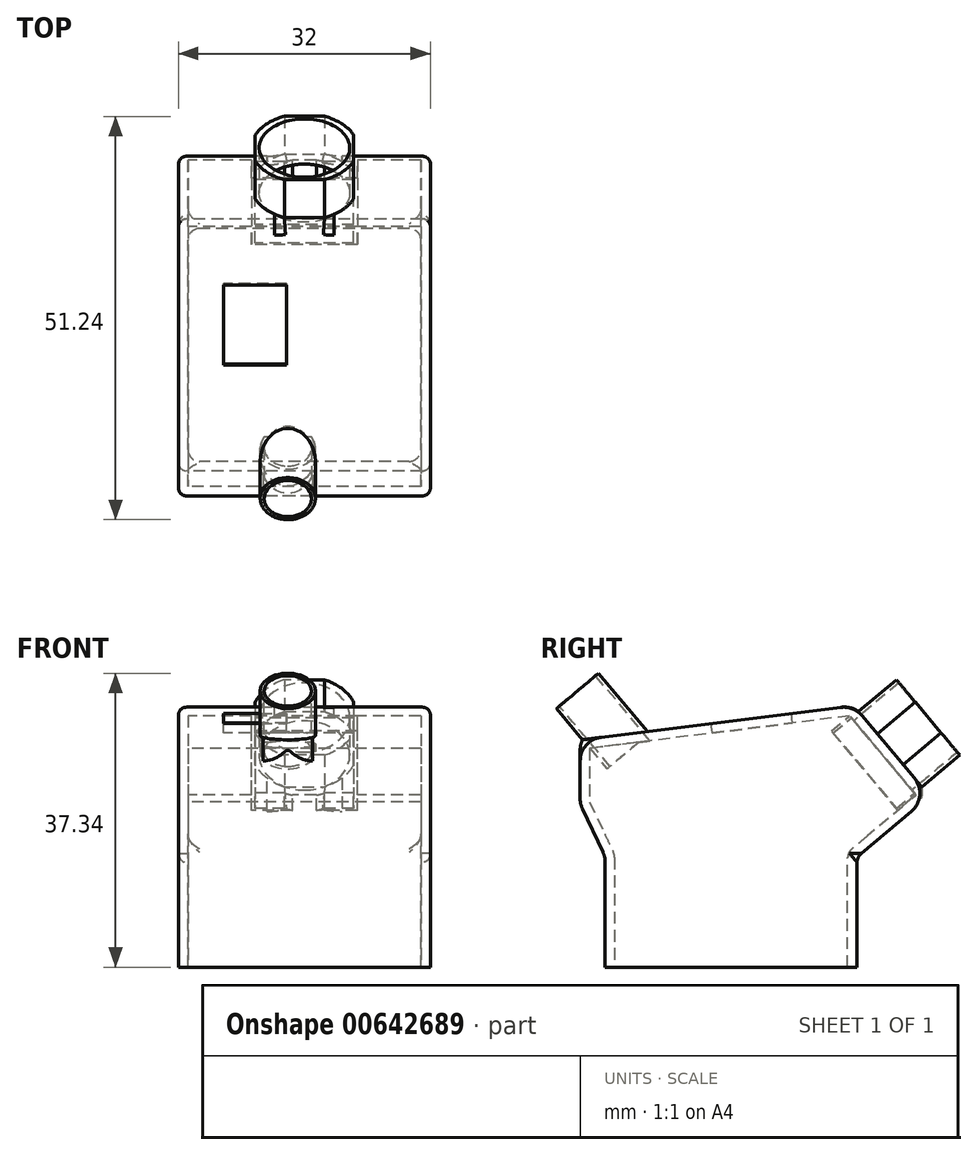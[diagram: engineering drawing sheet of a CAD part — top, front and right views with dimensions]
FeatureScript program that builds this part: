
annotation { "Feature Type Name" : "Feature", "Feature Type Description" : "" }
export const myFeature = defineFeature(function(context is Context, id is Id, definition is map)
    precondition{}
    {
        {
            var Q0;
            Q0=qCreatedBy(makeId("Right.planeOp"),FACE);
            var sketch = newSketch(context, id + "F0", { "sketchPlane" : qUnion([Q0])});
            skLineSegment(sketch, "E0", {"start": v(-20.8, -5.59) * mm, "end": v(11.2, -5.59) * mm});
            skLineSegment(sketch, "E1", {"start": v(11.2, -5.59) * mm, "end": v(11.2, 8.41) * mm});
            skLineSegment(sketch, "E2", {"start": v(-20.8, 8.41) * mm, "end": v(-20.8, -5.59) * mm});
            skLineSegment(sketch, "E3", {"start": v(10.74, 27.62) * mm, "end": v(20.39, 16.12) * mm});
            skLineSegment(sketch, "E4", {"start": v(20.39, 16.12) * mm, "end": v(11.2, 8.41) * mm});
            skLineSegment(sketch, "E5", {"start": v(-20.8, 8.41) * mm, "end": v(23.26, 8.41) * mm, "construction": true});
            skLineSegment(sketch, "E6", {"start": v(10.74, 27.62) * mm, "end": v(-23.98, 23.26) * mm});
            skLineSegment(sketch, "E7", {"start": v(-23.98, 23.26) * mm, "end": v(-23.98, 15.14) * mm});
            skLineSegment(sketch, "E8", {"start": v(-23.98, 15.14) * mm, "end": v(-20.8, 8.41) * mm});
            skSolve(sketch);
        }
        {
            var Q0;
            Q0=makeQuery(id+"F0.imprint","IMPRINT",FACE,{"disambiguationData":[TD([[makeQuery(id+"F0.imprint","IMPRINT",EDGE,{"derivedFrom":sQuery(id+"F0.wireOp",EDGE,"E0")}),1.0]])]});
            extrude(context, id + "F1", {"entities" : qUnion([Q0]), "depth" : 32 * mm, "offsetDistance" : 25 * mm});
        }
        {
            var Q0;
            Q0=makeQuery(id+"F1.opExtrude","SWEPT_FACE",FACE,{"disambiguationData":[OSD([sQuery(id+"F0.wireOp",EDGE,"E0")])]});
            shell(context, id + "F2", {"entities" : qUnion([Q0]), "thickness" : 1.2 * mm});
        }
        {
            var Q0;
            Q0=makeQuery(id+"F2.opShell","OFFSET_FACE",FACE,{"disambiguationData":[OSD([sQuery(id+"F0.wireOp",EDGE,"E3")])]});
            var sketch = newSketch(context, id + "F3", { "sketchPlane" : qUnion([Q0])});
            skCircle(sketch, "E9", {"center": v(16, 7.02) * mm, "radius": 5.75 * mm});
            skPoint(sketch, "E9.centerSnap0", {"position": v(16, 13.6) * mm});
            skPoint(sketch, "E9.centerSnap1", {"position": v(1.2, 7.02) * mm});
            skCircle(sketch, "E10.0", {"center": v(16, 7.02) * mm, "radius": 6.75 * mm});
            skLineSegment(sketch, "E11.0", {"start": v(-3.8, 18.6) * mm, "end": v(-3.8, -4.55) * mm});
            skLineSegment(sketch, "E11.1", {"start": v(35.8, 18.6) * mm, "end": v(-3.8, 18.6) * mm});
            skLineSegment(sketch, "E11.2", {"start": v(35.8, -4.55) * mm, "end": v(35.8, 18.6) * mm});
            skLineSegment(sketch, "E11.3", {"start": v(-3.8, -4.55) * mm, "end": v(35.8, -4.55) * mm});
            skLineSegment(sketch, "E12.bottom", {"start": v(22.25, 13.27) * mm, "end": v(9.75, 13.27) * mm});
            skLineSegment(sketch, "E12.top", {"start": v(22.25, 0.77) * mm, "end": v(9.75, 0.77) * mm});
            skLineSegment(sketch, "E12.left", {"start": v(22.25, 13.27) * mm, "end": v(22.25, 0.77) * mm});
            skLineSegment(sketch, "E12.right", {"start": v(9.75, 13.27) * mm, "end": v(9.75, 0.77) * mm});
            skLineSegment(sketch, "E13.bottom", {"start": v(22.75, 0.27) * mm, "end": v(9.25, 0.27) * mm});
            skLineSegment(sketch, "E13.top", {"start": v(22.75, 13.77) * mm, "end": v(9.25, 13.77) * mm});
            skLineSegment(sketch, "E13.left", {"start": v(22.75, 0.27) * mm, "end": v(22.75, 13.77) * mm});
            skLineSegment(sketch, "E13.right", {"start": v(9.25, 0.27) * mm, "end": v(9.25, 13.77) * mm});
            skSolve(sketch);
        }
        {
            var Q0;
            Q0=makeQuery(id+"F3.imprint","IMPRINT",FACE,{"disambiguationData":[TD([[makeQuery(id+"F3.imprint","IMPRINT",EDGE,{"derivedFrom":sQuery(id+"F3.wireOp",EDGE,"E9")}),1.0]])]});
            extrude(context, id + "F4", {"entities" : qUnion([Q0]), "operationType" : NewBodyOperationType.REMOVE, "oppositeDirection" : true, "depth" : 25 * mm, "offsetDistance" : 25 * mm});
        }
        {
            var Q0;
            Q0=makeQuery(id+"F3.imprint","IMPRINT",FACE,{"disambiguationData":[TD([[makeQuery(id+"F3.imprint","IMPRINT",EDGE,{"derivedFrom":sQuery(id+"F3.wireOp",EDGE,"E9")}),-1.0]])]});
            extrude(context, id + "F5", {"entities" : qUnion([Q0]), "operationType" : NewBodyOperationType.ADD, "oppositeDirection" : true, "depth" : 7.5 * mm, "offsetDistance" : 25 * mm});
        }
        {
            var Q0;
            Q0=makeQuery(id+"F1.opExtrude","SWEPT_EDGE",EDGE,{"disambiguationData":[OSD([sQuery(id+"F0.wireOp",EDGE,"E6"),sQuery(id+"F0.wireOp",EDGE,"E7")])]});
            cPlane(context, id + "F6", {"entities" : qUnion([Q0]), "cplaneType" : CPlaneType.LINE_ANGLE, "offset" : 25 * mm, "angle" : 50 * degree, "width" : 150 * mm, "height" : 150 * mm});
        }
        {
            var Q0;
            Q0=qCreatedBy(id+"F6.planeOp",FACE);
            var sketch = newSketch(context, id + "F7", { "sketchPlane" : qUnion([Q0])});
            skCircle(sketch, "E14", {"center": v(13.89, 0.33) * mm, "radius": 3 * mm});
            skCircle(sketch, "E15", {"center": v(13.89, 0.33) * mm, "radius": 3.5 * mm});
            skSolve(sketch);
        }
        {
            var Q0;
            Q0=makeQuery(id+"F7.imprint","IMPRINT",FACE,{"disambiguationData":[TD([[makeQuery(id+"F7.imprint","IMPRINT",EDGE,{"derivedFrom":sQuery(id+"F7.wireOp",EDGE,"E14")}),1.0]])]});
            extrude(context, id + "F8", {"entities" : qUnion([Q0]), "operationType" : NewBodyOperationType.REMOVE, "oppositeDirection" : true, "depth" : 10 * mm, "offsetDistance" : 25 * mm});
        }
        {
            var Q0;
            Q0=makeQuery(id+"F7.imprint","IMPRINT",FACE,{"disambiguationData":[TD([[makeQuery(id+"F7.imprint","IMPRINT",EDGE,{"derivedFrom":sQuery(id+"F7.wireOp",EDGE,"E14")}),-1.0]])]});
            extrude(context, id + "F9", {"entities" : qUnion([Q0]), "operationType" : NewBodyOperationType.ADD, "endBound" : BoundingType.SYMMETRIC, "depth" : 10 * mm, "offsetDistance" : 25 * mm});
        }
        {
            var Q0;
            Q0=makeQuery(id+"F1.opExtrude","SWEPT_EDGE",EDGE,{"disambiguationData":[OSD([sQuery(id+"F0.wireOp",EDGE,"E3"),sQuery(id+"F0.wireOp",EDGE,"E6")])]});
            var Q1;
            Q1=makeQuery(id+"F1.opExtrude","SWEPT_EDGE",EDGE,{"disambiguationData":[OSD([sQuery(id+"F0.wireOp",EDGE,"E3"),sQuery(id+"F0.wireOp",EDGE,"E4")])]});
            var Q2;
            Q2=makeQuery(id+"F1.opExtrude","SWEPT_EDGE",EDGE,{"disambiguationData":[OSD([sQuery(id+"F0.wireOp",EDGE,"E2"),sQuery(id+"F0.wireOp",EDGE,"E8")])]});
            var Q3;
            Q3=makeQuery(id+"F1.opExtrude","SWEPT_EDGE",EDGE,{"disambiguationData":[OSD([sQuery(id+"F0.wireOp",EDGE,"E7"),sQuery(id+"F0.wireOp",EDGE,"E8")])]});
            var Q4;
            Q4=makeQuery(id+"F1.opExtrude","SWEPT_EDGE",EDGE,{"disambiguationData":[OSD([sQuery(id+"F0.wireOp",EDGE,"E6"),sQuery(id+"F0.wireOp",EDGE,"E7")])]});
            fillet(context, id + "F10", {"entities" : qUnion([Q0, Q1, Q2, Q3, Q4]), "radius" : 3 * mm, "tangentPropagation" : true, "allowEdgeOverflow" : false});
        }
        {
            var Q0;
            Q0=makeQuery(id+"F1.opExtrude","CAP_EDGE",EDGE,{"disambiguationData":[OSD([sQuery(id+"F0.wireOp",EDGE,"E1")])],"isStart":true});
            var Q1;
            Q1=makeQuery(id+"F1.opExtrude","CAP_EDGE",EDGE,{"disambiguationData":[OSD([sQuery(id+"F0.wireOp",EDGE,"E4")])],"isStart":true});
            var Q2;
            Q2=makeQuery(id+"F1.opExtrude","CAP_EDGE",EDGE,{"disambiguationData":[OSD([sQuery(id+"F0.wireOp",EDGE,"E1")])],"isStart":false});
            var Q3;
            Q3=makeQuery(id+"F1.opExtrude","CAP_EDGE",EDGE,{"disambiguationData":[OSD([sQuery(id+"F0.wireOp",EDGE,"E4")])],"isStart":false});
            fillet(context, id + "F11", {"entities" : qUnion([Q0, Q1, Q2, Q3]), "radius" : 1 * mm, "tangentPropagation" : true, "allowEdgeOverflow" : false});
        }
        {
            var Q0;
            {var subQ0=sQuery(id+"F0.wireOp",EDGE,"E1");Q0=makeQuery(id+"F2.opShell","OFFSET_EDGE",EDGE,{"disambiguationData":[OSD([subQ0]),TDD([makeQuery(id+"F1.opExtrude","CAP_EDGE",EDGE,{"disambiguationData":[OSD([subQ0])],"isStart":false})])]});}
            var Q1;
            {var subQ0=sQuery(id+"F0.wireOp",EDGE,"E2");Q1=makeQuery(id+"F2.opShell","OFFSET_EDGE",EDGE,{"disambiguationData":[OSD([subQ0]),TDD([makeQuery(id+"F1.opExtrude","CAP_EDGE",EDGE,{"disambiguationData":[OSD([subQ0])],"isStart":false})])]});}
            var Q2;
            {var subQ0=sQuery(id+"F0.wireOp",EDGE,"E2");Q2=makeQuery(id+"F2.opShell","OFFSET_EDGE",EDGE,{"disambiguationData":[OSD([subQ0]),TDD([makeQuery(id+"F1.opExtrude","CAP_EDGE",EDGE,{"disambiguationData":[OSD([subQ0])],"isStart":true})])]});}
            var Q3;
            {var subQ0=sQuery(id+"F0.wireOp",EDGE,"E1");Q3=makeQuery(id+"F2.opShell","OFFSET_EDGE",EDGE,{"disambiguationData":[OSD([subQ0]),TDD([makeQuery(id+"F1.opExtrude","CAP_EDGE",EDGE,{"disambiguationData":[OSD([subQ0])],"isStart":true})])]});}
            var Q4;
            Q4=makeQuery(id+"F2.opShell","OFFSET_EDGE",EDGE,{"disambiguationData":[OSD([sQuery(id+"F0.wireOp",EDGE,"E1"),sQuery(id+"F0.wireOp",EDGE,"E4")])]});
            var Q5;
            Q5=makeQuery(id+"F2.opShell","OFFSET_EDGE",EDGE,{"disambiguationData":[OSD([sQuery(id+"F0.wireOp",EDGE,"E2"),sQuery(id+"F0.wireOp",EDGE,"E8")])]});
            var Q6;
            Q6=makeQuery(id+"F1.opExtrude","SWEPT_EDGE",EDGE,{"disambiguationData":[OSD([sQuery(id+"F0.wireOp",EDGE,"E1"),sQuery(id+"F0.wireOp",EDGE,"E4")])]});
            fillet(context, id + "F12", {"entities" : qUnion([Q0, Q1, Q2, Q3, Q4, Q5, Q6]), "radius" : 1.5 * mm, "tangentPropagation" : true, "allowEdgeOverflow" : false});
        }
        {
            var Q0;
            Q0=makeQuery(id+"F1.opExtrude","SWEPT_FACE",FACE,{"disambiguationData":[OSD([sQuery(id+"F0.wireOp",EDGE,"E6")])]});
            var sketch = newSketch(context, id + "F13", { "sketchPlane" : qUnion([Q0])});
            skLineSegment(sketch, "E16.bottom", {"start": v(5.7, 6.12) * mm, "end": v(13.76, 6.12) * mm});
            skLineSegment(sketch, "E16.top", {"start": v(5.7, -4.14) * mm, "end": v(13.76, -4.14) * mm});
            skLineSegment(sketch, "E16.left", {"start": v(5.7, 6.12) * mm, "end": v(5.7, -4.14) * mm});
            skLineSegment(sketch, "E16.right", {"start": v(13.76, 6.12) * mm, "end": v(13.76, -4.14) * mm});
            skPoint(sketch, "E16.middle", {"position": v(9.73, 0.99) * mm});
            skSolve(sketch);
        }
        {
            var Q0;
            Q0 = qSketchRegion(id + "F13", true);
            extrude(context, id + "F14", {"entities" : qUnion([Q0]), "operationType" : NewBodyOperationType.REMOVE, "oppositeDirection" : true, "depth" : 5 * mm, "offsetDistance" : 25 * mm});
        }
        {
            var Q0;
            {var subQ0=sQuery(id+"F3.wireOp",EDGE,"E12.right");var subQ3=sQuery(id+"F3.wireOp",EDGE,"E10.0");var subQ4=makeQuery(id+"F3.imprint","INTERSECT",VERTEX,{"disambiguationData":[OD(0.0)],"derivedFrom":[subQ3,subQ0]});Q0=makeQuery(id+"F3.imprint","IMPRINT",FACE,{"disambiguationData":[TD([[makeQuery(id+"F3.imprint","IMPRINT",EDGE,{"disambiguationData":[TD([[subQ4,-1.0]])],"derivedFrom":subQ3}),-1.0]])]});}
            var Q1;
            {var subQ0=sQuery(id+"F3.wireOp",EDGE,"E12.bottom");var subQ1=sQuery(id+"F3.wireOp",EDGE,"E10.0");var subQ2=makeQuery(id+"F3.imprint","INTERSECT",VERTEX,{"disambiguationData":[OD(0.0)],"derivedFrom":[subQ1,subQ0]});Q1=makeQuery(id+"F3.imprint","IMPRINT",FACE,{"disambiguationData":[TD([[makeQuery(id+"F3.imprint","IMPRINT",EDGE,{"disambiguationData":[TD([[subQ2,-1.0]])],"derivedFrom":subQ0}),-1.0]])]});}
            var Q2;
            {var subQ0=sQuery(id+"F3.wireOp",EDGE,"E12.left");var subQ3=sQuery(id+"F3.wireOp",EDGE,"E10.0");var subQ4=makeQuery(id+"F3.imprint","INTERSECT",VERTEX,{"disambiguationData":[OD(0.0)],"derivedFrom":[subQ3,subQ0]});Q2=makeQuery(id+"F3.imprint","IMPRINT",FACE,{"disambiguationData":[TD([[makeQuery(id+"F3.imprint","IMPRINT",EDGE,{"disambiguationData":[TD([[subQ4,1.0]])],"derivedFrom":subQ3}),-1.0]])]});}
            var Q3;
            {var subQ0=sQuery(id+"F3.wireOp",EDGE,"E12.right");var subQ1=sQuery(id+"F3.wireOp",EDGE,"E10.0");var subQ2=makeQuery(id+"F3.imprint","INTERSECT",VERTEX,{"disambiguationData":[OD(0.0)],"derivedFrom":[subQ1,subQ0]});Q3=makeQuery(id+"F3.imprint","IMPRINT",FACE,{"disambiguationData":[TD([[makeQuery(id+"F3.imprint","IMPRINT",EDGE,{"disambiguationData":[TD([[subQ2,-1.0]])],"derivedFrom":subQ1}),1.0]])]});}
            var Q4;
            {var subQ3=sQuery(id+"F3.wireOp",EDGE,"E10.0");var subQ8=sQuery(id+"F3.wireOp",EDGE,"E13.right");var subQ10=makeQuery(id+"F3.imprint","INTERSECT",VERTEX,{"derivedFrom":[subQ3,subQ8]});Q4=makeQuery(id+"F3.imprint","IMPRINT",FACE,{"disambiguationData":[TD([[makeQuery(id+"F3.imprint","IMPRINT",EDGE,{"disambiguationData":[TD([[subQ10,-1.0]])],"derivedFrom":subQ3}),-1.0]])]});}
            var Q5;
            {var subQ0=sQuery(id+"F3.wireOp",EDGE,"E12.left");var subQ1=sQuery(id+"F3.wireOp",EDGE,"E10.0");var subQ2=makeQuery(id+"F3.imprint","INTERSECT",VERTEX,{"disambiguationData":[OD(0.0)],"derivedFrom":[subQ1,subQ0]});Q5=makeQuery(id+"F3.imprint","IMPRINT",FACE,{"disambiguationData":[TD([[makeQuery(id+"F3.imprint","IMPRINT",EDGE,{"disambiguationData":[TD([[subQ2,1.0]])],"derivedFrom":subQ1}),1.0]])]});}
            var Q6;
            {var subQ0=sQuery(id+"F3.wireOp",EDGE,"E13.left");var subQ1=sQuery(id+"F3.wireOp",EDGE,"E10.0");var subQ2=makeQuery(id+"F3.imprint","INTERSECT",VERTEX,{"derivedFrom":[subQ1,subQ0]});Q6=makeQuery(id+"F3.imprint","IMPRINT",FACE,{"disambiguationData":[TD([[makeQuery(id+"F3.imprint","IMPRINT",EDGE,{"disambiguationData":[TD([[subQ2,1.0]])],"derivedFrom":subQ1}),-1.0]])]});}
            var Q7;
            {var subQ0=sQuery(id+"F3.wireOp",EDGE,"E12.top");var subQ1=sQuery(id+"F3.wireOp",EDGE,"E10.0");var subQ2=makeQuery(id+"F3.imprint","INTERSECT",VERTEX,{"disambiguationData":[OD(0.0)],"derivedFrom":[subQ1,subQ0]});Q7=makeQuery(id+"F3.imprint","IMPRINT",FACE,{"disambiguationData":[TD([[makeQuery(id+"F3.imprint","IMPRINT",EDGE,{"disambiguationData":[TD([[subQ2,1.0]])],"derivedFrom":subQ0}),1.0]])]});}
            extrude(context, id + "F15", {"entities" : qUnion([Q0, Q1, Q2, Q3, Q4, Q5, Q6, Q7]), "operationType" : NewBodyOperationType.ADD, "depth" : 3 * mm, "offsetDistance" : 25 * mm});
        }
    });
